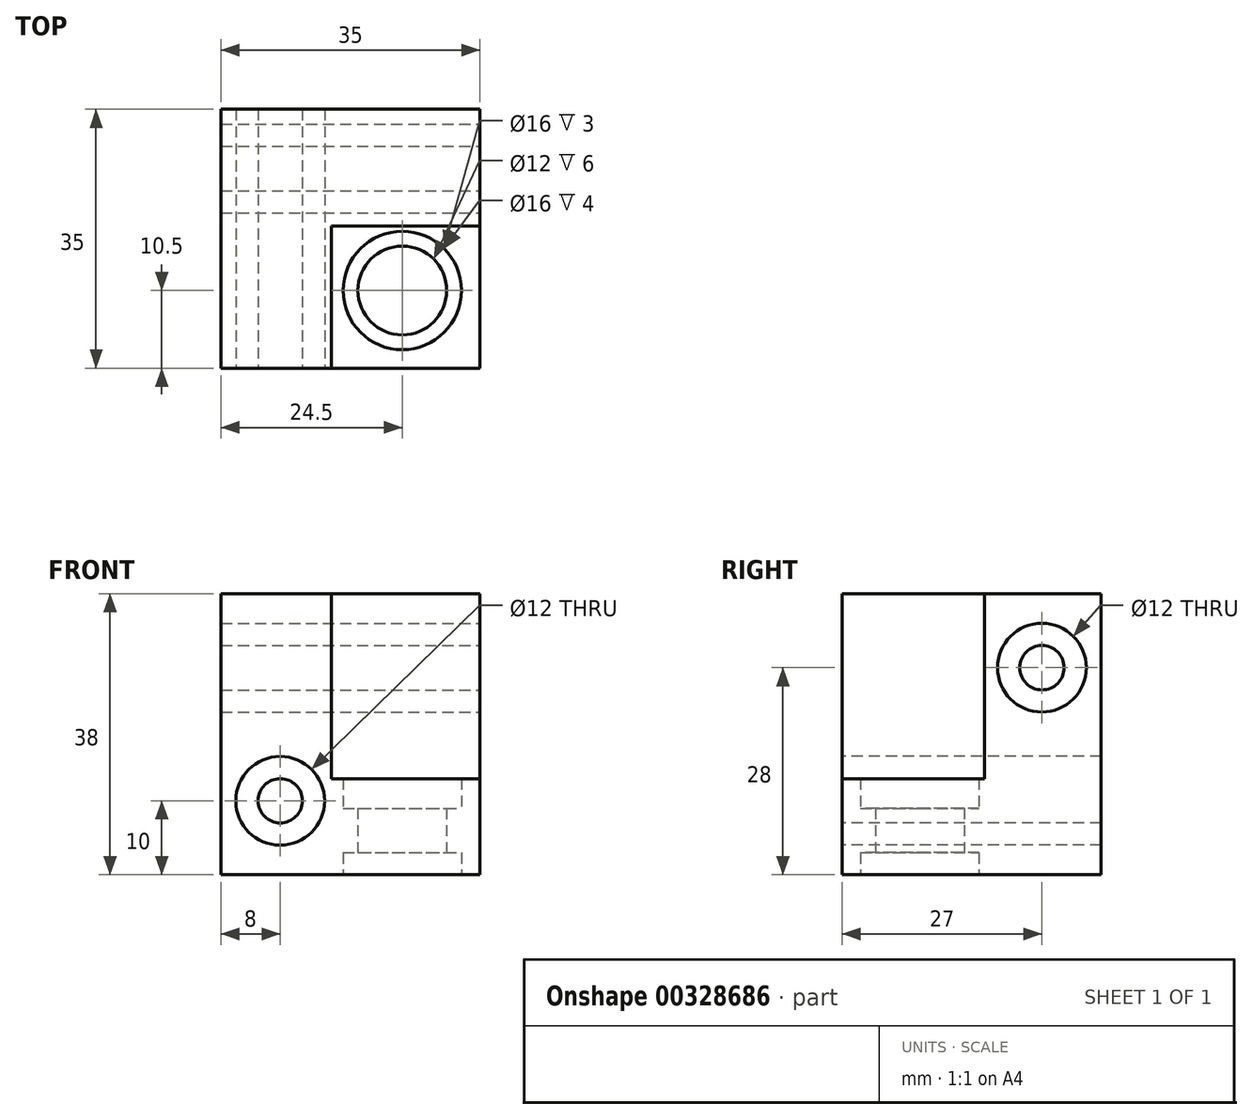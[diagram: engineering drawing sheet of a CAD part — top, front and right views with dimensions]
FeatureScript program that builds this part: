
annotation { "Feature Type Name" : "Feature", "Feature Type Description" : "" }
export const myFeature = defineFeature(function(context is Context, id is Id, definition is map)
    precondition{}
    {
        {
            var Q0;
            Q0=qCreatedBy(makeId("Right.planeOp"),FACE);
            var sketch = newSketch(context, id + "F0", { "sketchPlane" : qUnion([Q0])});
            skCircle(sketch, "E0", {"center": v(9.5, 0) * mm, "radius": 6 * mm});
            skLineSegment(sketch, "E1", {"start": v(17.5, 10.72) * mm, "end": v(17.5, -17.7) * mm, "construction": true});
            skCircle(sketch, "E2", {"center": v(9.5, 0) * mm, "radius": 3 * mm});
            skSolve(sketch);
        }
        {
            var Q0;
            Q0 = qSketchRegion(id + "F0", true);
            extrude(context, id + "F1", {"entities" : qUnion([Q0]), "oppositeDirection" : true, "depth" : 17.5 * mm, "hasSecondDirection" : true, "secondDirectionOppositeDirection" : false, "secondDirectionDepth" : 17.5 * mm});
        }
        {
            var Q0;
            Q0=qCreatedBy(makeId("Front.planeOp"),FACE);
            var sketch = newSketch(context, id + "F2", { "sketchPlane" : qUnion([Q0])});
            skCircle(sketch, "E3", {"center": v(-9.5, -18) * mm, "radius": 6 * mm});
            skLineSegment(sketch, "E4", {"start": v(-17.5, -10.32) * mm, "end": v(-17.5, -27.12) * mm, "construction": true});
            skCircle(sketch, "E5", {"center": v(-9.5, -18) * mm, "radius": 3 * mm});
            skSolve(sketch);
        }
        {
            var Q0;
            Q0 = qSketchRegion(id + "F2", true);
            extrude(context, id + "F3", {"entities" : qUnion([Q0]), "oppositeDirection" : true, "depth" : 17.5 * mm, "hasSecondDirection" : true, "secondDirectionOppositeDirection" : false, "secondDirectionDepth" : 17.5 * mm});
        }
        {
            var Q0;
            Q0=qCreatedBy(makeId("Top.planeOp"),FACE);
            cPlane(context, id + "F4", {"entities" : qUnion([Q0]), "cplaneType" : CPlaneType.OFFSET, "offset" : 28 * mm, "oppositeDirection" : true, "width" : 150 * mm, "height" : 150 * mm});
        }
        {
            var Q0;
            Q0=qCreatedBy(id+"F4.planeOp",FACE);
            var sketch = newSketch(context, id + "F5", { "sketchPlane" : qUnion([Q0])});
            skCircle(sketch, "E6", {"center": v(7, -7) * mm, "radius": 8 * mm, "construction": true});
            skCircle(sketch, "E7", {"center": v(7, -7) * mm, "radius": 6 * mm, "construction": true});
            skLineSegment(sketch, "E8.bottom", {"start": v(-17.5, 17.5) * mm, "end": v(17.5, 17.5) * mm});
            skLineSegment(sketch, "E8.top", {"start": v(-17.5, -17.5) * mm, "end": v(17.5, -17.5) * mm});
            skLineSegment(sketch, "E8.left", {"start": v(-17.5, 17.5) * mm, "end": v(-17.5, -17.5) * mm});
            skLineSegment(sketch, "E8.right", {"start": v(17.5, 17.5) * mm, "end": v(17.5, -17.5) * mm});
            skCircle(sketch, "E9", {"center": v(-1.2, 1.2) * mm, "radius": 2 * mm, "construction": true});
            skCircle(sketch, "E10", {"center": v(-1.2, 1.2) * mm, "radius": 3.45 * mm, "construction": true});
            skCircle(sketch, "E11.cCircle", {"center": v(7, -7) * mm, "radius": 5 * mm, "construction": true});
            skLineSegment(sketch, "E11.0", {"start": v(9.89, -12) * mm, "end": v(4.11, -12) * mm, "construction": true});
            skLineSegment(sketch, "E11.1", {"start": v(4.11, -12) * mm, "end": v(1.23, -7) * mm, "construction": true});
            skLineSegment(sketch, "E11.2", {"start": v(1.23, -7) * mm, "end": v(4.11, -2) * mm, "construction": true});
            skLineSegment(sketch, "E11.3", {"start": v(4.11, -2) * mm, "end": v(9.89, -2) * mm, "construction": true});
            skLineSegment(sketch, "E11.4", {"start": v(9.89, -2) * mm, "end": v(12.77, -7) * mm, "construction": true});
            skLineSegment(sketch, "E11.5", {"start": v(12.77, -7) * mm, "end": v(9.89, -12) * mm, "construction": true});
            skPoint(sketch, "E11.0.midPoint", {"position": v(7, -12) * mm});
            skSolve(sketch);
        }
        {
            var Q0;
            Q0=sQuery(id+"F5.wireOp",VERTEX,"E6.center");
            var Q1;
            Q1=qCreatedBy(makeId("Front.planeOp"),FACE);
            cPlane(context, id + "F6", {"entities" : qUnion([Q0, Q1]), "cplaneType" : CPlaneType.PLANE_POINT, "offset" : 25 * mm, "width" : 150 * mm, "height" : 150 * mm});
        }
        {
            var Q0;
            Q0=qCreatedBy(id+"F6.planeOp",FACE);
            var sketch = newSketch(context, id + "F7", { "sketchPlane" : qUnion([Q0])});
            skLineSegment(sketch, "E12.0", {"start": v(1, -28) * mm, "end": v(13, -28) * mm});
            skLineSegment(sketch, "E13.0", {"start": v(-1, -28) * mm, "end": v(15, -28) * mm});
            skLineSegment(sketch, "E14.0", {"start": v(1, -28) * mm, "end": v(13, -28) * mm, "construction": true});
            skLineSegment(sketch, "E15.0", {"start": v(-1, -28) * mm, "end": v(15, -28) * mm, "construction": true});
            skLineSegment(sketch, "E16", {"start": v(7, -28) * mm, "end": v(7, -6.1) * mm, "construction": true});
            skLineSegment(sketch, "E17", {"start": v(15, -28) * mm, "end": v(15, -25) * mm});
            skLineSegment(sketch, "E18", {"start": v(15, -25) * mm, "end": v(13, -25) * mm});
            skLineSegment(sketch, "E19", {"start": v(13, -25) * mm, "end": v(13, -19) * mm});
            skLineSegment(sketch, "E20", {"start": v(13, -19) * mm, "end": v(15, -19) * mm});
            skLineSegment(sketch, "E21", {"start": v(15, -19) * mm, "end": v(15, -15) * mm});
            skLineSegment(sketch, "E22", {"start": v(15, -15) * mm, "end": v(7, -15) * mm});
            skLineSegment(sketch, "E23", {"start": v(7, -15) * mm, "end": v(7, -28) * mm});
            skSolve(sketch);
        }
        {
            var Q0;
            Q0 = qSketchRegion(id + "F7", true);
            var Q1;
            Q1=sQuery(id+"F7.wireOp",EDGE,"E16");
            revolve(context, id + "F8", {"entities" : qUnion([Q0]), "axis" : qUnion([Q1]), "revolveType" : RevolveType.FULL});
        }
        {
            var Q0;
            Q0=makeQuery(id+"F5.imprint","IMPRINT",FACE,{"disambiguationData":[TD([[makeQuery(id+"F5.imprint","IMPRINT",EDGE,{"derivedFrom":sQuery(id+"F5.wireOp",EDGE,"E8.bottom")}),-1.0]])]});
            var Q1;
            Q1=sQuery(id+"F5.wireOp",EDGE,"E8.left");
            var Q2;
            Q2=sQuery(id+"F5.wireOp",EDGE,"E8.top");
            var Q3;
            Q3=sQuery(id+"F5.wireOp",EDGE,"E8.right");
            var Q4;
            Q4=sQuery(id+"F5.wireOp",EDGE,"E8.bottom");
            var Q5;
            Q5=makeQuery(id+"F8.opRevolve","SWEPT_FACE",FACE,{"disambiguationData":[OSD([sQuery(id+"F7.wireOp",EDGE,"E22")])]});
            extrude(context, id + "F9", {"entities" : qUnion([Q0]), "surfaceEntities" : qUnion([Q1, Q2, Q3, Q4]), "endBoundEntityFace" : qUnion([Q5]), "depth" : 38 * mm});
        }
        {
            var Q0;
            Q0=makeQuery(id+"F8.opRevolve","SWEPT_BODY",BODY,{"disambiguationData":[OSD([sQuery(id+"F7.wireOp",EDGE,"E13.0"),sQuery(id+"F7.wireOp",EDGE,"E17"),sQuery(id+"F7.wireOp",EDGE,"E18"),sQuery(id+"F7.wireOp",EDGE,"E19"),sQuery(id+"F7.wireOp",EDGE,"E20"),sQuery(id+"F7.wireOp",EDGE,"E21"),sQuery(id+"F7.wireOp",EDGE,"E22"),sQuery(id+"F7.wireOp",EDGE,"E23")])]});
            var Q1;
            Q1=makeQuery(id+"F9.opExtrude","SWEPT_BODY",BODY,{"disambiguationData":[OSD([sQuery(id+"F5.wireOp",EDGE,"E8.bottom"),sQuery(id+"F5.wireOp",EDGE,"E8.top"),sQuery(id+"F5.wireOp",EDGE,"E8.left"),sQuery(id+"F5.wireOp",EDGE,"E8.right")])]});
            booleanBodies(context, id + "F10", {"operationType" : BooleanOperationType.SUBTRACTION, "tools" : qUnion([Q0]), "targets" : qUnion([Q1])});
        }
        {
            var Q0;
            Q0=makeQuery(id+"F9.opExtrude","CAP_FACE",FACE,{"disambiguationData":[OSD([sQuery(id+"F5.wireOp",EDGE,"E8.bottom"),sQuery(id+"F5.wireOp",EDGE,"E8.top"),sQuery(id+"F5.wireOp",EDGE,"E8.left"),sQuery(id+"F5.wireOp",EDGE,"E8.right")])],"isStart":false});
            var sketch = newSketch(context, id + "F11", { "sketchPlane" : qUnion([Q0])});
            skLineSegment(sketch, "E24.bottom", {"start": v(17.5, -17.5) * mm, "end": v(-2.58, -17.5) * mm});
            skLineSegment(sketch, "E24.left", {"start": v(17.5, -17.5) * mm, "end": v(17.5, 1.72) * mm});
            skLineSegment(sketch, "E24.right", {"start": v(-2.58, -17.5) * mm, "end": v(-2.58, 1.72) * mm});
            skLineSegment(sketch, "E25", {"start": v(17.5, 1.72) * mm, "end": v(-2.58, 1.72) * mm});
            skSolve(sketch);
        }
        {
            var Q0;
            Q0 = qSketchRegion(id + "F11", true);
            extrude(context, id + "F12", {"entities" : qUnion([Q0]), "operationType" : NewBodyOperationType.REMOVE, "oppositeDirection" : true, "depth" : 25 * mm});
        }
        {
            var Q0;
            Q0=makeQuery(id+"F3.opExtrude","SWEPT_BODY",BODY,{"disambiguationData":[OSD([sQuery(id+"F2.wireOp",EDGE,"E3"),sQuery(id+"F2.wireOp",EDGE,"E5")])]});
            var Q1;
            Q1=makeQuery(id+"F1.opExtrude","SWEPT_BODY",BODY,{"disambiguationData":[OSD([sQuery(id+"F0.wireOp",EDGE,"E0"),sQuery(id+"F0.wireOp",EDGE,"E2")])]});
            var Q2;
            Q2=makeQuery(id+"F9.opExtrude","SWEPT_BODY",BODY,{"disambiguationData":[OSD([sQuery(id+"F5.wireOp",EDGE,"E8.bottom"),sQuery(id+"F5.wireOp",EDGE,"E8.top"),sQuery(id+"F5.wireOp",EDGE,"E8.left"),sQuery(id+"F5.wireOp",EDGE,"E8.right")])]});
            booleanBodies(context, id + "F13", {"operationType" : BooleanOperationType.SUBTRACTION, "tools" : qUnion([Q0, Q1]), "targets" : qUnion([Q2])});
        }
    });
